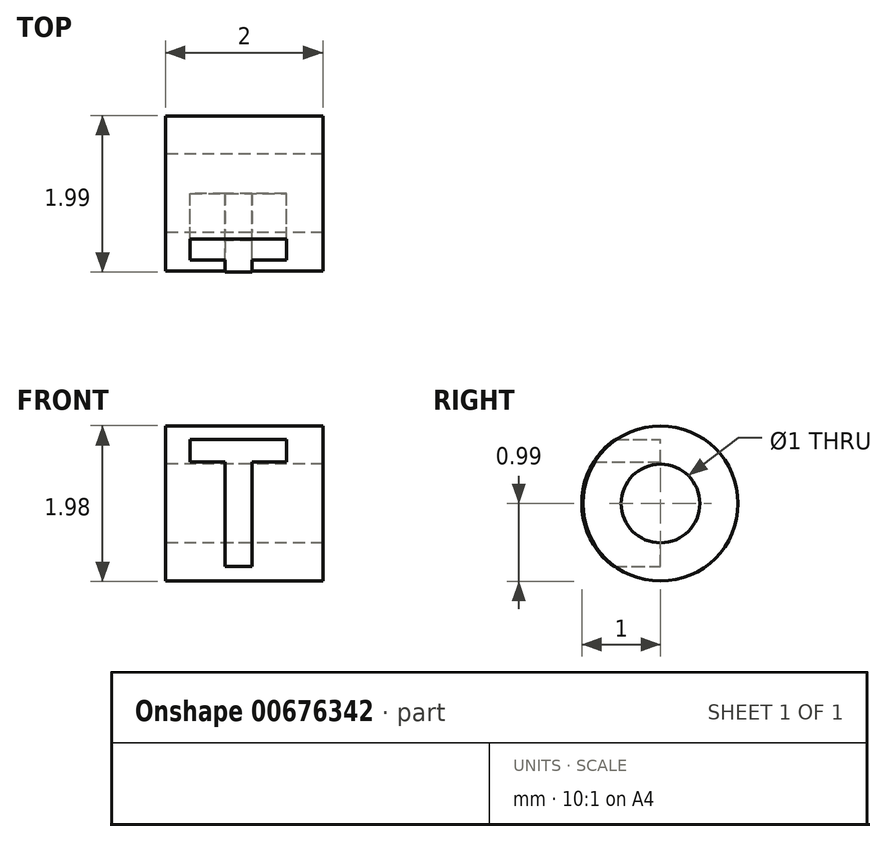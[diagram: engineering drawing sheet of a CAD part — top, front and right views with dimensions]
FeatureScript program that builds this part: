
annotation { "Feature Type Name" : "Feature", "Feature Type Description" : "" }
export const myFeature = defineFeature(function(context is Context, id is Id, definition is map)
    precondition{}
    {
        {
            var Q0;
            Q0=qCreatedBy(makeId("Right.planeOp"),FACE);
            var sketch = newSketch(context, id + "F0", { "sketchPlane" : qUnion([Q0])});
            skCircle(sketch, "E0", {"center": v(0, 0) * mm, "radius": 0.5 * mm});
            skCircle(sketch, "E1", {"center": v(0, 0) * mm, "radius": 1 * mm});
            skCircle(sketch, "E2", {"center": v(0, 0) * mm, "radius": 0.98 * mm});
            skSolve(sketch);
        }
        {
            var Q0;
            Q0=makeQuery(id+"F0.imprint","IMPRINT",FACE,{"disambiguationData":[TD([[makeQuery(id+"F0.imprint","IMPRINT",EDGE,{"derivedFrom":sQuery(id+"F0.wireOp",EDGE,"E0")}),-1.0]])]});
            var Q1;
            Q1=makeQuery(id+"F0.imprint","IMPRINT",FACE,{"disambiguationData":[TD([[makeQuery(id+"F0.imprint","IMPRINT",EDGE,{"derivedFrom":sQuery(id+"F0.wireOp",EDGE,"E1")}),1.0]])]});
            extrude(context, id + "F1", {"entities" : qUnion([Q0, Q1]), "depth" : 2 * mm, "offsetDistance" : 25 * mm});
        }
        {
            var Q0;
            Q0=qCreatedBy(makeId("Front.planeOp"),FACE);
            var sketch = newSketch(context, id + "F2", { "sketchPlane" : qUnion([Q0])});
            skText(sketch, "E3", { "text": "T", "fontName": "OpenSans-Bold.ttf"});
            const initialGuessF2  = {"E3": [0.00027, -0.0008, 1, 0, 0.00163]};
            skSetInitialGuess(sketch, initialGuessF2);
            skSolve(sketch);
        }
        {
            var Q0;
            Q0=qSketchRegion(id+"F2",true);
            var Q1;
            Q1=qConstructionFilter(qBodyType(qCreatedBy(id+"F2",EDGE),BodyType.WIRE),ConstructionObject.NO);
            var Q2;
            Q2=makeQuery(id+"F1.opExtrude","SWEPT_FACE",FACE,{"disambiguationData":[OSD([sQuery(id+"F0.wireOp",EDGE,"E1")])]});
            var Q3;
            Q3=makeQuery(id+"F1.opExtrude","SWEPT_BODY",BODY,{"disambiguationData":[OSD([sQuery(id+"F0.wireOp",EDGE,"E0"),sQuery(id+"F0.wireOp",EDGE,"E1")])]});
            var Q4;
            Q4=sQuery(id+"F0.wireOp",VERTEX,"27635d6e-dcd6-4653-b727-4819003c0945");
            extrude(context, id + "F3", {"entities" : qUnion([Q0]), "operationType" : NewBodyOperationType.INTERSECT, "surfaceEntities" : qUnion([Q1]), "endBound" : BoundingType.UP_TO_SURFACE, "endBoundEntityFace" : qUnion([Q2]), "endBoundEntityBody" : qUnion([Q3]), "endBoundEntityVertex" : qUnion([Q4]), "depth" : 25 * mm, "offsetDistance" : 25 * mm});
        }
        {
            var Q0;
            Q0=makeQuery(id+"F0.imprint","IMPRINT",FACE,{"disambiguationData":[TD([[makeQuery(id+"F0.imprint","IMPRINT",EDGE,{"derivedFrom":sQuery(id+"F0.wireOp",EDGE,"E0")}),-1.0]])]});
            extrude(context, id + "F4", {"entities" : qUnion([Q0]), "depth" : 2 * mm, "offsetDistance" : 25 * mm});
        }
    });
